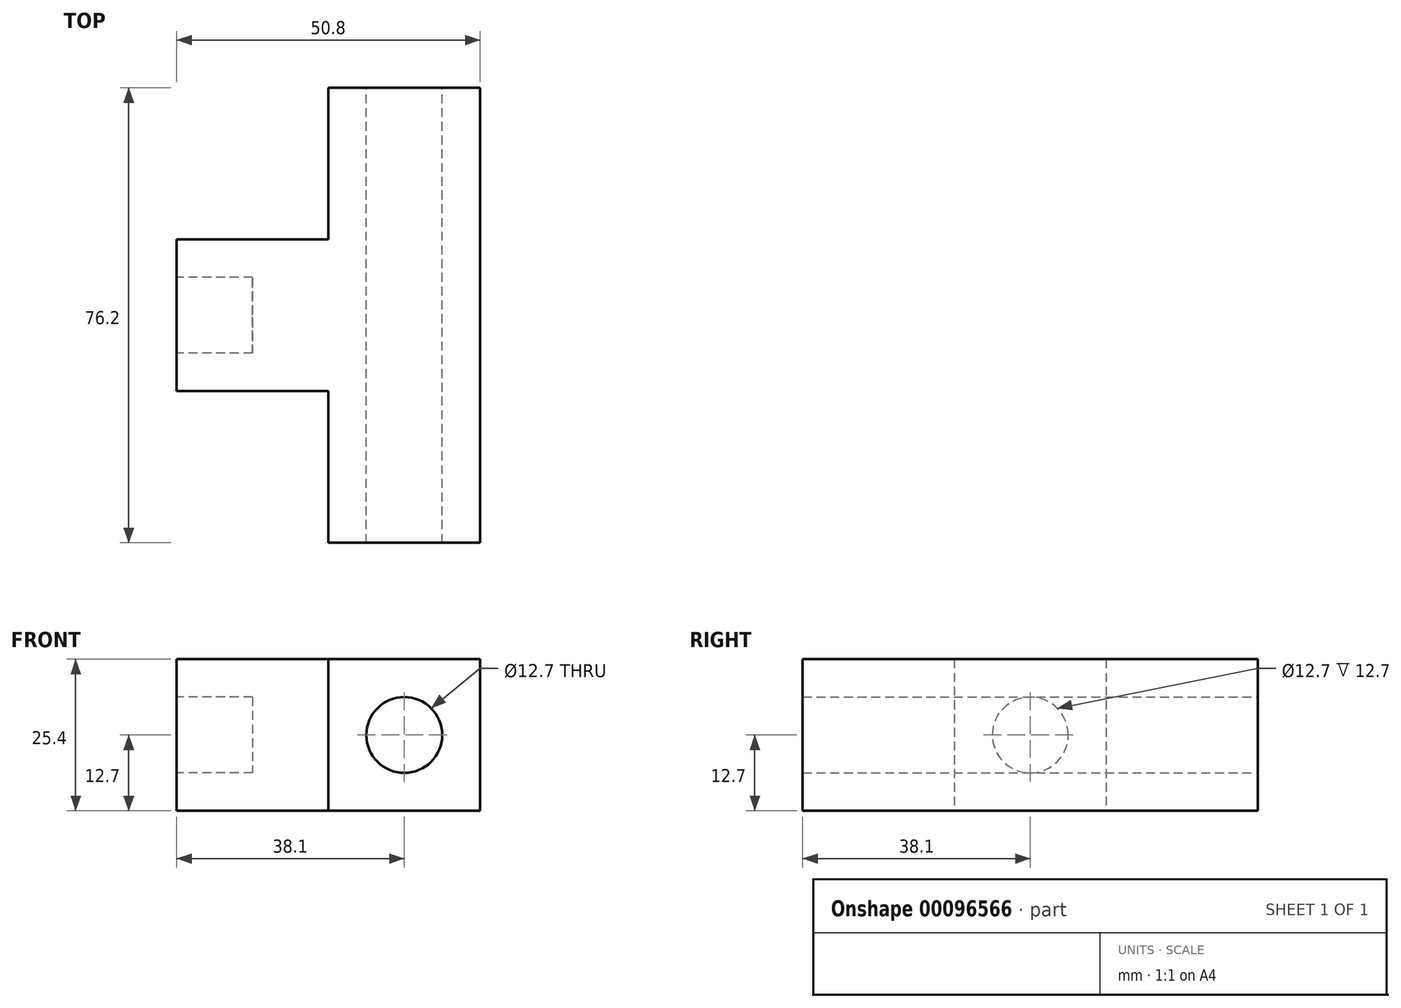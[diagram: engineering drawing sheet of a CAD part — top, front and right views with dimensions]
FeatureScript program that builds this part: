
annotation { "Feature Type Name" : "Feature", "Feature Type Description" : "" }
export const myFeature = defineFeature(function(context is Context, id is Id, definition is map)
    precondition{}
    {
        {
            var Q0;
            Q0=qCreatedBy(makeId("Top.planeOp"),FACE);
            var sketch = newSketch(context, id + "F0", { "sketchPlane" : qUnion([Q0])});
            skLineSegment(sketch, "E0", {"start": v(12.7, 0) * mm, "end": v(12.7, 38.1) * mm});
            skLineSegment(sketch, "E1", {"start": v(12.7, 38.1) * mm, "end": v(-12.7, 38.1) * mm});
            skLineSegment(sketch, "E2", {"start": v(-12.7, 38.1) * mm, "end": v(-12.7, 12.7) * mm});
            skLineSegment(sketch, "E3", {"start": v(-12.7, 12.7) * mm, "end": v(-38.1, 12.7) * mm});
            skLineSegment(sketch, "E4", {"start": v(-38.1, 12.7) * mm, "end": v(-38.1, 0) * mm});
            skLineSegment(sketch, "E5.MirrorCS", {"start": v(-12.7, -38.1) * mm, "end": v(-12.7, -12.7) * mm});
            skLineSegment(sketch, "E6.MirrorCS", {"start": v(-38.1, -12.7) * mm, "end": v(-38.1, 0) * mm});
            skLineSegment(sketch, "E7.MirrorCS", {"start": v(-12.7, -12.7) * mm, "end": v(-38.1, -12.7) * mm});
            skLineSegment(sketch, "E8.MirrorCS", {"start": v(12.7, 0) * mm, "end": v(12.7, -38.1) * mm});
            skLineSegment(sketch, "E9.MirrorCS", {"start": v(12.7, -38.1) * mm, "end": v(-12.7, -38.1) * mm});
            skSolve(sketch);
        }
        {
            var Q0;
            Q0 = qSketchRegion(id + "F0", true);
            extrude(context, id + "F1", {"entities" : qUnion([Q0]), "depth" : 25.4 * mm, "symmetric" : true});
        }
        {
            var Q0;
            Q0=makeQuery(id+"F1.opExtrude","SWEPT_FACE",FACE,{"disambiguationData":[OSD([sQuery(id+"F0.wireOp",EDGE,"E1")])]});
            var sketch = newSketch(context, id + "F2", { "sketchPlane" : qUnion([Q0])});
            skLineSegment(sketch, "E10", {"start": v(-5.56, 0) * mm, "end": v(5.24, 0) * mm, "construction": true});
            skLineSegment(sketch, "E11", {"start": v(0, -4.63) * mm, "end": v(0, 6.7) * mm, "construction": true});
            skCircle(sketch, "E12", {"center": v(0, 0) * mm, "radius": 6.35 * mm});
            skSolve(sketch);
        }
        {
            var Q0;
            Q0 = qSketchRegion(id + "F2", true);
            extrude(context, id + "F3", {"entities" : qUnion([Q0]), "operationType" : NewBodyOperationType.REMOVE, "endBound" : BoundingType.THROUGH_ALL, "oppositeDirection" : true, "depth" : 25.4 * mm});
        }
        {
            var Q0;
            Q0=makeQuery(id+"F1.opExtrude","SWEPT_FACE",FACE,{"disambiguationData":[OSD([sQuery(id+"F0.wireOp",EDGE,"E4"),sQuery(id+"F0.wireOp",EDGE,"E6.MirrorCS")])]});
            var sketch = newSketch(context, id + "F4", { "sketchPlane" : qUnion([Q0])});
            skCircle(sketch, "E13", {"center": v(0, 0) * mm, "radius": 6.35 * mm});
            skSolve(sketch);
        }
        {
            var Q0;
            Q0 = qSketchRegion(id + "F4", true);
            extrude(context, id + "F5", {"entities" : qUnion([Q0]), "operationType" : NewBodyOperationType.REMOVE, "oppositeDirection" : true, "depth" : 12.7 * mm});
        }
    });
